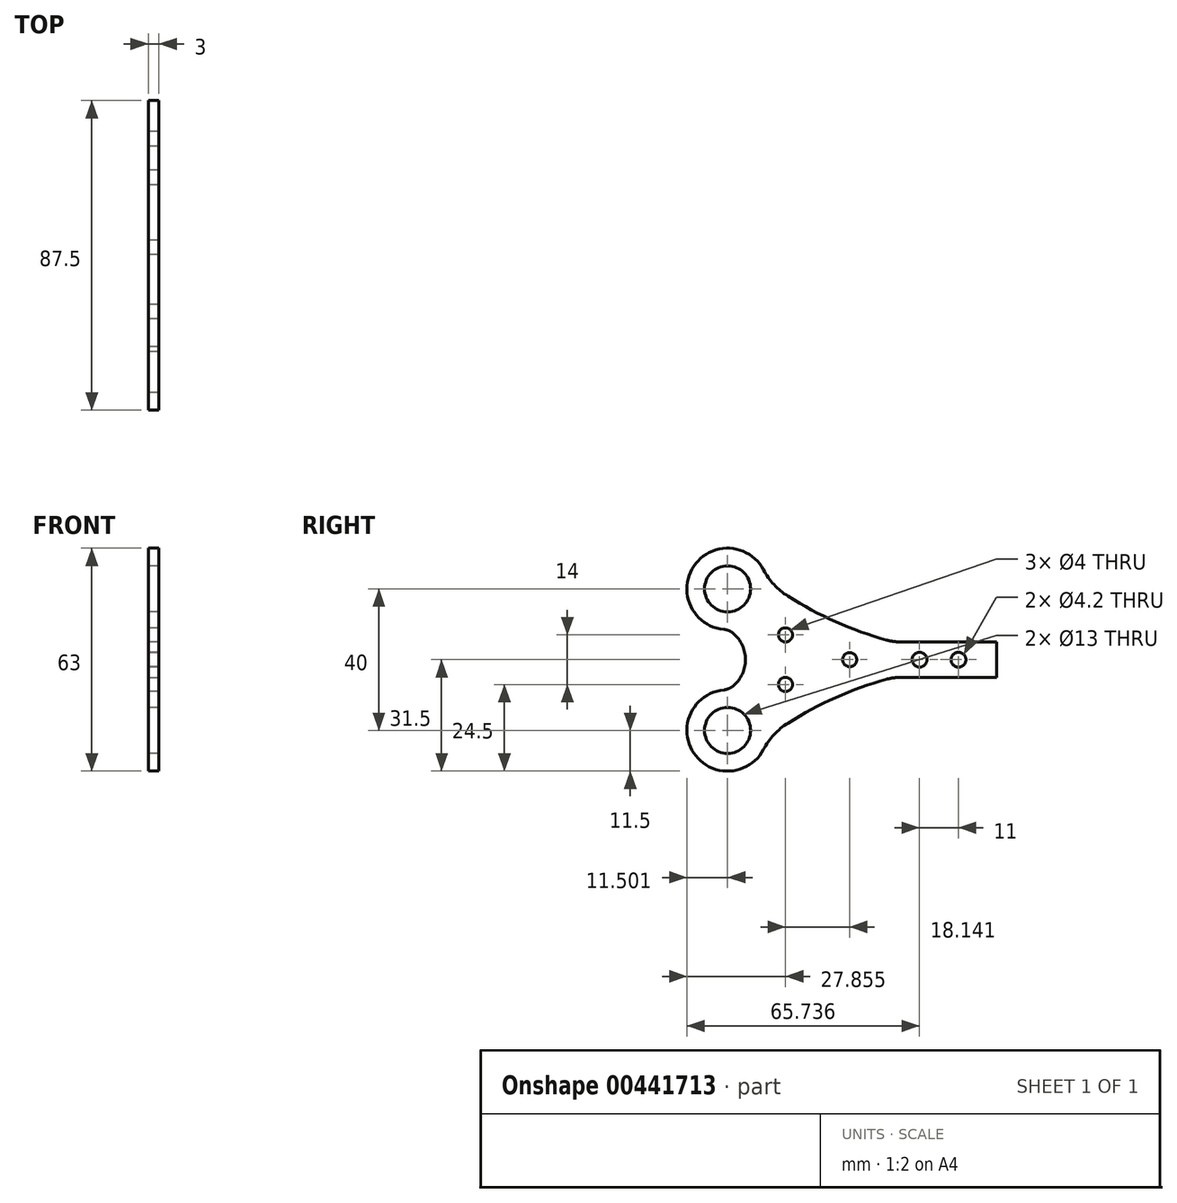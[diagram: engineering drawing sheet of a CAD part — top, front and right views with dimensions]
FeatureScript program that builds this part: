
annotation { "Feature Type Name" : "Feature", "Feature Type Description" : "" }
export const myFeature = defineFeature(function(context is Context, id is Id, definition is map)
    precondition{}
    {
        {
            var Q0;
            Q0=qCreatedBy(makeId("Right.planeOp"),FACE);
            var sketch = newSketch(context, id + "F0", { "sketchPlane" : qUnion([Q0])});
            skCircle(sketch, "E0", {"center": v(4.6, 20) * mm, "radius": 11.5 * mm});
            skLineSegment(sketch, "E1", {"start": v(0, 54.17) * mm, "end": v(0, -43.27) * mm, "construction": true});
            skLineSegment(sketch, "E2", {"start": v(-70.18, 0) * mm, "end": v(98.02, 0) * mm, "construction": true});
            skCircle(sketch, "E3", {"center": v(58.83, 0) * mm, "radius": 2.1 * mm});
            skArc(sketch, "E4", {"start": v(4.6, 31.5) * mm, "mid": v(26.33, 15.13) * mm, "end": v(51.59, 5) * mm});
            skCircle(sketch, "E5", {"center": v(4.6, 20) * mm, "radius": 6.5 * mm});
            skCircle(sketch, "E6.MirrorC", {"center": v(4.6, -20) * mm, "radius": 11.5 * mm});
            skCircle(sketch, "E7.MirrorC", {"center": v(4.6, -20) * mm, "radius": 6.5 * mm});
            skArc(sketch, "E8.MirrorCS", {"start": v(4.6, -31.5) * mm, "mid": v(26.33, -15.13) * mm, "end": v(51.59, -5) * mm});
            skLineSegment(sketch, "E9", {"start": v(51.59, 5) * mm, "end": v(80.59, 5) * mm});
            skLineSegment(sketch, "E10", {"start": v(80.59, 5) * mm, "end": v(80.59, -5) * mm});
            skLineSegment(sketch, "E11", {"start": v(80.59, -5) * mm, "end": v(51.59, -5) * mm});
            skLineSegment(sketch, "E12", {"start": v(4.6, 57.27) * mm, "end": v(4.6, -43.54) * mm, "construction": true});
            skArc(sketch, "E13", {"start": v(4.6, -8.5) * mm, "mid": v(9.66, 0) * mm, "end": v(4.6, 8.5) * mm});
            skLineSegment(sketch, "E14", {"start": v(51.59, 5) * mm, "end": v(51.59, -5) * mm, "construction": true});
            skCircle(sketch, "E15", {"center": v(69.83, 0) * mm, "radius": 2.1 * mm});
            skCircle(sketch, "E16", {"center": v(20.95, 7) * mm, "radius": 2 * mm});
            skCircle(sketch, "E17.MirrorC", {"center": v(20.95, -7) * mm, "radius": 2 * mm});
            skCircle(sketch, "E18", {"center": v(39.09, 0) * mm, "radius": 2 * mm});
            skSolve(sketch);
        }
        {
            var Q0;
            Q0 = qSketchRegion(id + "F0", true);
            extrude(context, id + "F1", {"entities" : qUnion([Q0]), "endBound" : BoundingType.SYMMETRIC, "depth" : 3 * mm, "offsetDistance" : 25 * mm});
        }
        {
            var Q0;
            Q0=makeQuery(id+"F1.opExtrude","SWEPT_EDGE",EDGE,{"disambiguationData":[OSD([sQuery(id+"F0.wireOp",EDGE,"E8.MirrorCS"),sQuery(id+"F0.wireOp",EDGE,"E11")])]});
            var Q1;
            Q1=makeQuery(id+"F1.opExtrude","SWEPT_EDGE",EDGE,{"disambiguationData":[OSD([sQuery(id+"F0.wireOp",EDGE,"E4"),sQuery(id+"F0.wireOp",EDGE,"E9")])]});
            fillet(context, id + "F2", {"entities" : qUnion([Q0, Q1]), "radius" : 15 * mm, "tangentPropagation" : true, "allowEdgeOverflow" : false});
        }
        {
            var Q0;
            Q0=makeQuery(id+"F1.opExtrude","SWEPT_EDGE",EDGE,{"disambiguationData":[OSD([sQuery(id+"F0.wireOp",EDGE,"E6.MirrorC"),sQuery(id+"F0.wireOp",EDGE,"E8.MirrorCS")])]});
            var Q1;
            Q1=makeQuery(id+"F1.opExtrude","SWEPT_EDGE",EDGE,{"disambiguationData":[OSD([sQuery(id+"F0.wireOp",EDGE,"E0"),sQuery(id+"F0.wireOp",EDGE,"E4")])]});
            fillet(context, id + "F3", {"entities" : qUnion([Q0, Q1]), "radius" : 20 * mm, "tangentPropagation" : true, "allowEdgeOverflow" : false});
        }
        {
            var Q0;
            Q0=makeQuery(id+"F1.opExtrude","SWEPT_EDGE",EDGE,{"disambiguationData":[OSD([sQuery(id+"F0.wireOp",EDGE,"E0"),sQuery(id+"F0.wireOp",EDGE,"E13")])]});
            var Q1;
            Q1=makeQuery(id+"F1.opExtrude","SWEPT_EDGE",EDGE,{"disambiguationData":[OSD([sQuery(id+"F0.wireOp",EDGE,"E6.MirrorC"),sQuery(id+"F0.wireOp",EDGE,"E13")])]});
            fillet(context, id + "F4", {"entities" : qUnion([Q0, Q1]), "radius" : 5 * mm, "tangentPropagation" : true, "allowEdgeOverflow" : false});
        }
    });
